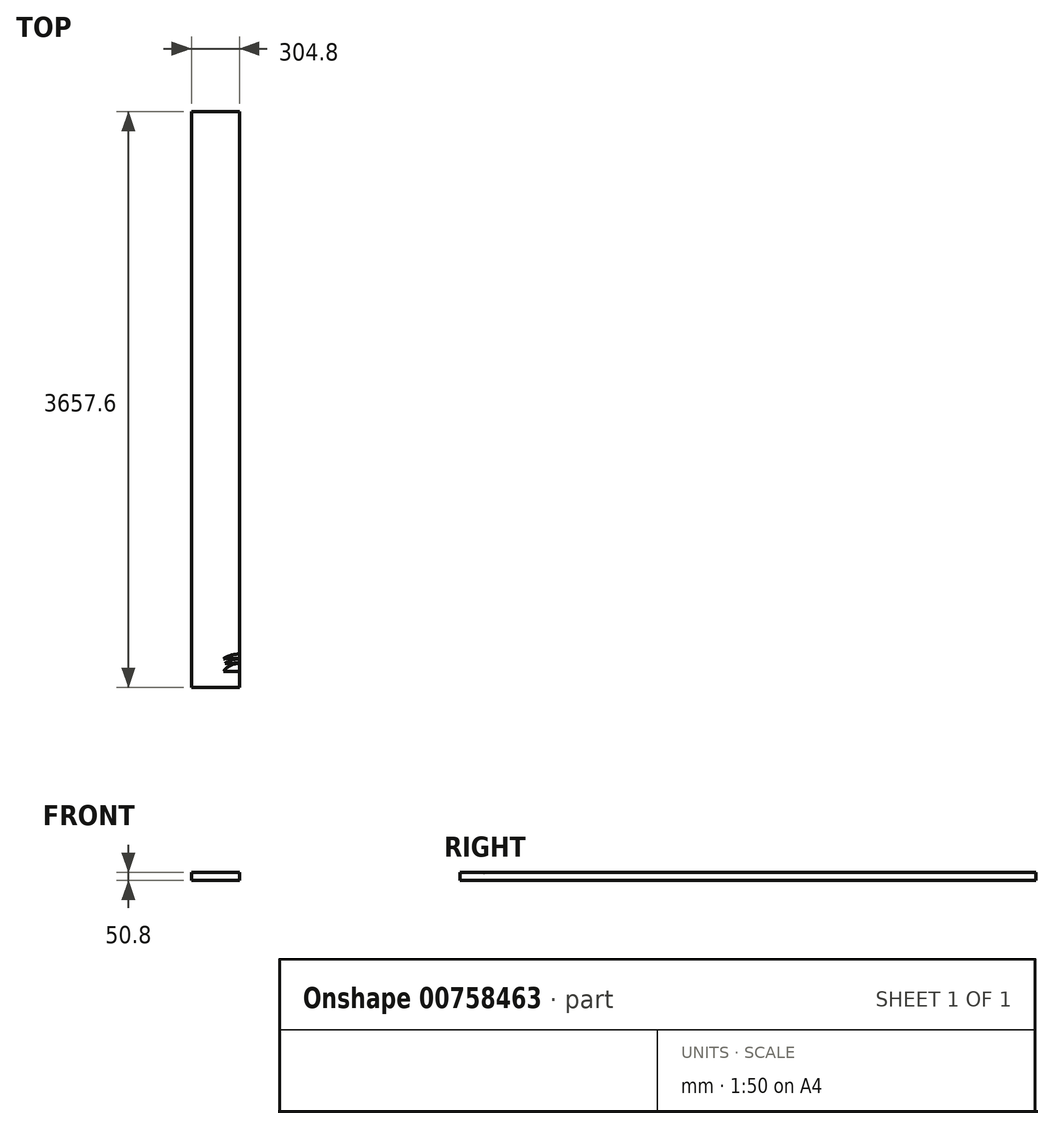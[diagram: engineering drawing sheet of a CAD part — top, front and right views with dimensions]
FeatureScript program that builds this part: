
annotation { "Feature Type Name" : "Feature", "Feature Type Description" : "" }
export const myFeature = defineFeature(function(context is Context, id is Id, definition is map)
    precondition{}
    {
        {
            var Q0;
            Q0=qCreatedBy(makeId("Top.planeOp"),FACE);
            var sketch = newSketch(context, id + "F0", { "sketchPlane" : qUnion([Q0])});
            skLineSegment(sketch, "E0.bottom", {"start": v(-152.4, 1828.8) * mm, "end": v(152.4, 1828.8) * mm});
            skLineSegment(sketch, "E0.top", {"start": v(-152.4, -1828.8) * mm, "end": v(152.4, -1828.8) * mm});
            skLineSegment(sketch, "E0.left", {"start": v(-152.4, 1828.8) * mm, "end": v(-152.4, -1828.8) * mm});
            skLineSegment(sketch, "E0.right", {"start": v(152.4, 1828.8) * mm, "end": v(152.4, -1828.8) * mm});
            skPoint(sketch, "E0.middle", {"position": v(0, 0) * mm});
            skSolve(sketch);
        }
        {
            var Q0;
            Q0 = qSketchRegion(id + "F0", true);
            extrude(context, id + "F1", {"entities" : qUnion([Q0]), "oppositeDirection" : true, "depth" : 50.8 * mm, "offsetDistance" : 25.4 * mm});
        }
        {
            var Q0;
            Q0=makeQuery(id+"F1.opExtrude","SWEPT_FACE",FACE,{"disambiguationData":[OSD([sQuery(id+"F0.wireOp",EDGE,"E0.right")])]});
            var sketch = newSketch(context, id + "F2", { "sketchPlane" : qUnion([Q0])});
            skLineSegment(sketch, "E1", {"start": v(-1726.93, 0) * mm, "end": v(-1676.18, -1.59) * mm});
            skLineSegment(sketch, "E2", {"start": v(-1676.18, -1.59) * mm, "end": v(-1676.13, 0) * mm});
            skLineSegment(sketch, "E3", {"start": v(-1726.93, 0) * mm, "end": v(-1676.13, 0) * mm});
            skLineSegment(sketch, "E4", {"start": v(-1674.82, 0) * mm, "end": v(-1647, -0.92) * mm});
            skLineSegment(sketch, "E5", {"start": v(-1647, -0.92) * mm, "end": v(-1646.97, 0) * mm});
            skLineSegment(sketch, "E6", {"start": v(-1674.82, 0) * mm, "end": v(-1646.97, 0) * mm});
            skLineSegment(sketch, "E7", {"start": v(-1645.03, 0) * mm, "end": v(-1617.21, -0.92) * mm});
            skLineSegment(sketch, "E8", {"start": v(-1617.21, -0.92) * mm, "end": v(-1617.18, 0) * mm});
            skLineSegment(sketch, "E9", {"start": v(-1645.03, 0) * mm, "end": v(-1617.18, 0) * mm});
            skSolve(sketch);
        }
        {
            var Q0;
            Q0=sQuery(id+"F2.wireOp",EDGE,"E1");
            cPlane(context, id + "F3", {"entities" : qUnion([Q0]), "cplaneType" : CPlaneType.LINE_ANGLE, "offset" : 25.4 * mm, "angle" : 0 * degree, "width" : 152.4 * mm, "height" : 152.4 * mm});
        }
        {
            var Q0;
            Q0=qCreatedBy(id+"F3.planeOp",FACE);
            var sketch = newSketch(context, id + "F4", { "sketchPlane" : qUnion([Q0])});
            skArc(sketch, "E10", {"start": v(152.4, -1675.3) * mm, "mid": v(85.69, -1694.24) * mm, "end": v(38.86, -1745.4) * mm});
            skLineSegment(sketch, "E11", {"start": v(152.4, -1675.3) * mm, "end": v(162.89, -1675.3) * mm});
            skSolve(sketch);
        }
        {
            var Q0;
            Q0 = qSketchRegion(id + "F2", true);
            var Q1;
            Q1=sQuery(id+"F4.wireOp",EDGE,"E10");
            sweep(context, id + "F5", {"operationType" : NewBodyOperationType.REMOVE, "profiles" : qUnion([Q0]), "path" : qUnion([Q1])});
        }
    });
